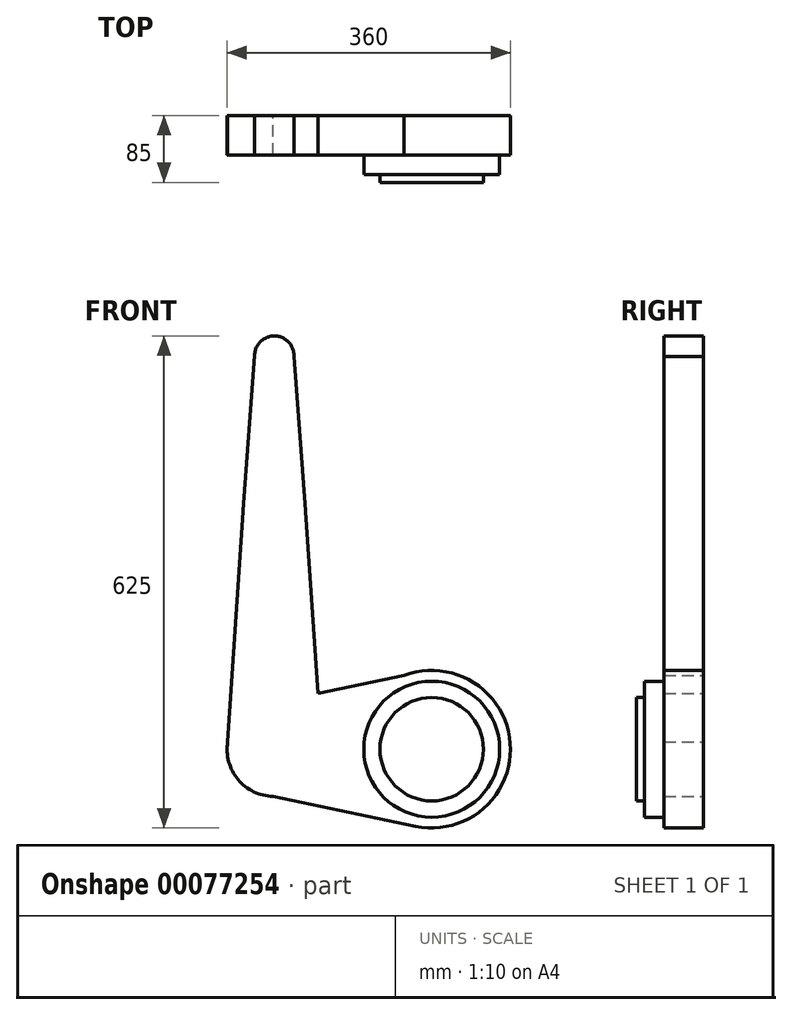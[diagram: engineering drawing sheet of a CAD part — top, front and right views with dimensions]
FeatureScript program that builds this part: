
annotation { "Feature Type Name" : "Feature", "Feature Type Description" : "" }
export const myFeature = defineFeature(function(context is Context, id is Id, definition is map)
    precondition{}
    {
        {
            var Q0;
            Q0=qCreatedBy(makeId("Front.planeOp"),FACE);
            var sketch = newSketch(context, id + "F0", { "sketchPlane" : qUnion([Q0])});
            skCircle(sketch, "E0", {"center": v(0, -100.9) * mm, "radius": 100 * mm});
            skCircle(sketch, "E1", {"center": v(-200, -100.9) * mm, "radius": 60 * mm});
            skCircle(sketch, "E2", {"center": v(-200, 199.1) * mm, "radius": 40 * mm});
            skCircle(sketch, "E3", {"center": v(-200, 399.1) * mm, "radius": 25 * mm});
            skLineSegment(sketch, "E4", {"start": v(-224.77, 402.47) * mm, "end": v(-239.89, 202.1) * mm});
            skLineSegment(sketch, "E5", {"start": v(-239.89, 202.1) * mm, "end": v(-259.98, -102.48) * mm});
            skLineSegment(sketch, "E6", {"start": v(-175.02, 398.17) * mm, "end": v(-160.12, 202.12) * mm});
            skLineSegment(sketch, "E7", {"start": v(-201.49, -160.9) * mm, "end": v(0, -203.08) * mm});
            skLineSegment(sketch, "E8", {"start": v(0, 0) * mm, "end": v(-197.5, -40.96) * mm});
            skLineSegment(sketch, "E9", {"start": v(-160.12, 202.12) * mm, "end": v(-140.13, -96.9) * mm});
            skSolve(sketch);
        }
        {
            var Q0;
            Q0 = qSketchRegion(id + "F0", true);
            extrude(context, id + "F1", {"entities" : qUnion([Q0]), "depth" : 50 * mm});
        }
        {
            var Q0;
            Q0=makeQuery(id+"F1.opExtrude","CAP_FACE",FACE,{"disambiguationData":[OSD([sQuery(id+"F0.wireOp",EDGE,"E0"),sQuery(id+"F0.wireOp",EDGE,"E1"),sQuery(id+"F0.wireOp",EDGE,"E2"),sQuery(id+"F0.wireOp",EDGE,"E3"),sQuery(id+"F0.wireOp",EDGE,"E4"),sQuery(id+"F0.wireOp",EDGE,"E5"),sQuery(id+"F0.wireOp",EDGE,"E6"),sQuery(id+"F0.wireOp",EDGE,"E7"),sQuery(id+"F0.wireOp",EDGE,"E8"),sQuery(id+"F0.wireOp",EDGE,"E9")])],"isStart":false});
            var sketch = newSketch(context, id + "F2", { "sketchPlane" : qUnion([Q0])});
            skCircle(sketch, "E10", {"center": v(0, -100.9) * mm, "radius": 86.32 * mm});
            skSolve(sketch);
        }
        {
            var Q0;
            Q0 = qSketchRegion(id + "F2", true);
            extrude(context, id + "F3", {"entities" : qUnion([Q0]), "operationType" : NewBodyOperationType.ADD, "depth" : 25 * mm});
        }
        {
            var Q0;
            Q0=makeQuery(id+"F3.opExtrude","CAP_FACE",FACE,{"disambiguationData":[OSD([sQuery(id+"F2.wireOp",EDGE,"E10")])],"isStart":false});
            var sketch = newSketch(context, id + "F4", { "sketchPlane" : qUnion([Q0])});
            skCircle(sketch, "E11", {"center": v(0, -100.9) * mm, "radius": 65.72 * mm});
            skSolve(sketch);
        }
        {
            var Q0;
            Q0 = qSketchRegion(id + "F4", true);
            extrude(context, id + "F5", {"entities" : qUnion([Q0]), "operationType" : NewBodyOperationType.ADD, "depth" : 10 * mm});
        }
    });
